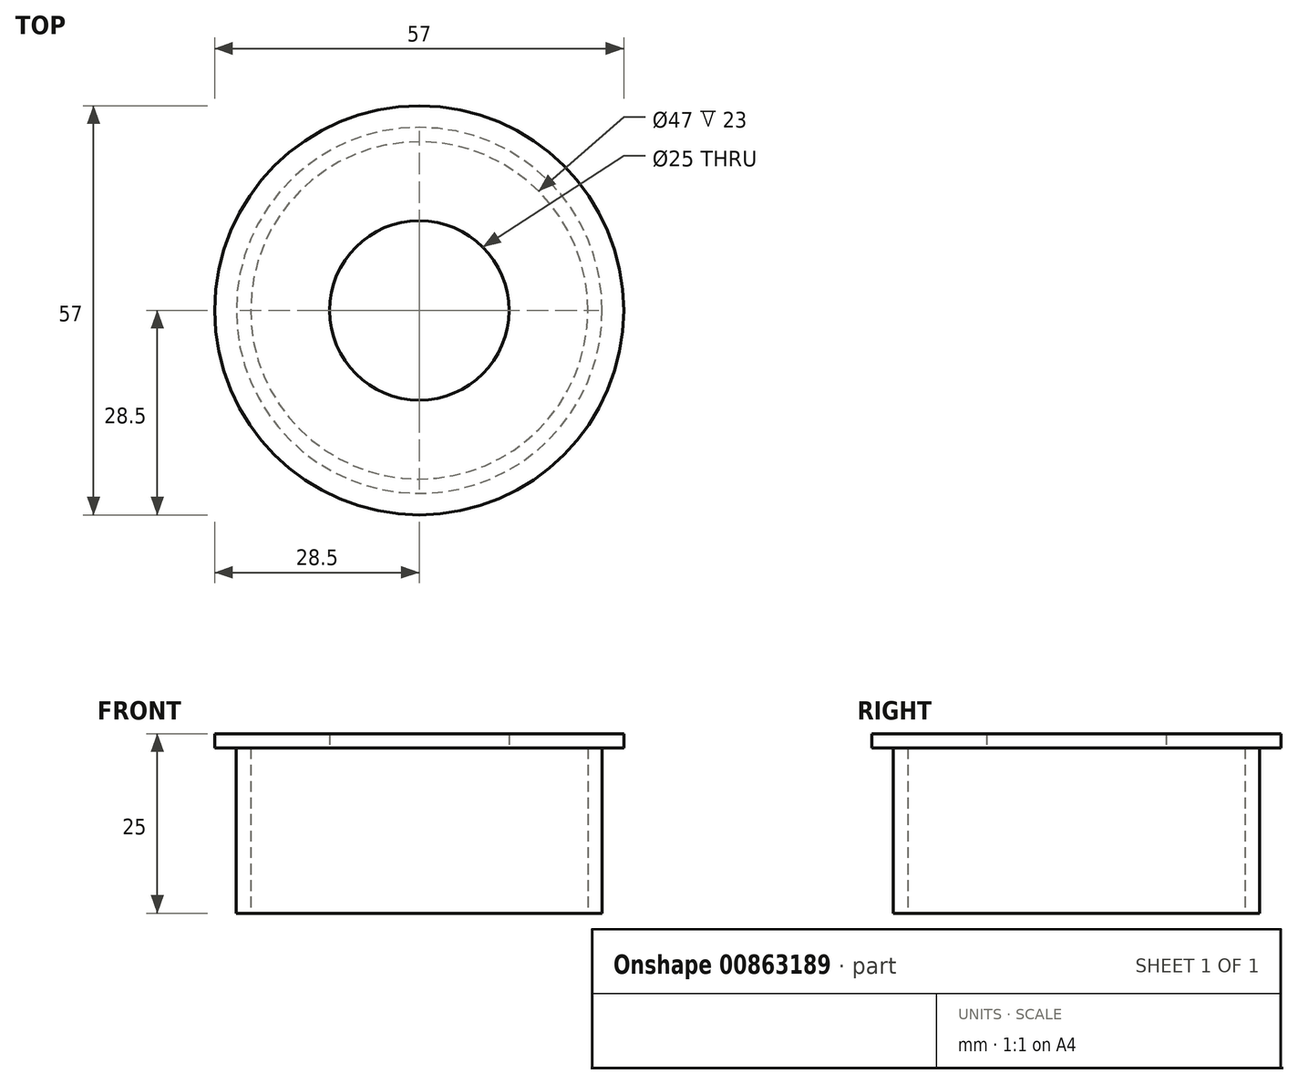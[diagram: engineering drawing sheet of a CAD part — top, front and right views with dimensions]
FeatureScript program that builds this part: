
annotation { "Feature Type Name" : "Feature", "Feature Type Description" : "" }
export const myFeature = defineFeature(function(context is Context, id is Id, definition is map)
    precondition{}
    {
        {
            var Q0;
            Q0=qCreatedBy(makeId("Top.planeOp"),FACE);
            var sketch = newSketch(context, id + "F0", { "sketchPlane" : qUnion([Q0])});
            skCircle(sketch, "E0", {"center": v(0, 0) * mm, "radius": 25.5 * mm});
            skCircle(sketch, "E1", {"center": v(0, 0) * mm, "radius": 12.5 * mm});
            skCircle(sketch, "E2.0", {"center": v(0, 0) * mm, "radius": 28.5 * mm});
            skSolve(sketch);
        }
        {
            var Q0;
            Q0=makeQuery(id+"F0.imprint","IMPRINT",FACE,{"disambiguationData":[TD([[makeQuery(id+"F0.imprint","IMPRINT",EDGE,{"derivedFrom":sQuery(id+"F0.wireOp",EDGE,"E0")}),1.0]])]});
            var Q1;
            Q1=makeQuery(id+"F0.imprint","IMPRINT",FACE,{"disambiguationData":[TD([[makeQuery(id+"F0.imprint","IMPRINT",EDGE,{"derivedFrom":sQuery(id+"F0.wireOp",EDGE,"E1")}),1.0]])]});
            extrude(context, id + "F1", {"entities" : qUnion([Q0, Q1]), "depth" : 25 * mm, "offsetDistance" : 25 * mm});
        }
        {
            var Q0;
            Q0=makeQuery(id+"F1.opExtrude","CAP_FACE",FACE,{"disambiguationData":[OSD([sQuery(id+"F0.wireOp",EDGE,"E0")])],"isStart":true});
            shell(context, id + "F2", {"entities" : qUnion([Q0]), "thickness" : 2 * mm});
        }
        {
            var Q0;
            Q0=makeQuery(id+"F0.imprint","IMPRINT",FACE,{"disambiguationData":[TD([[makeQuery(id+"F0.imprint","IMPRINT",EDGE,{"derivedFrom":sQuery(id+"F0.wireOp",EDGE,"E1")}),1.0]])]});
            var Q1;
            Q1=makeQuery(id+"F1.opExtrude","CAP_FACE",FACE,{"disambiguationData":[OSD([sQuery(id+"F0.wireOp",EDGE,"E0")])],"isStart":false});
            extrude(context, id + "F3", {"entities" : qUnion([Q0]), "operationType" : NewBodyOperationType.REMOVE, "endBound" : BoundingType.UP_TO_SURFACE, "depth" : 25 * mm, "endBoundEntityFace" : qUnion([Q1]), "offsetDistance" : 25 * mm});
        }
        {
            var Q0;
            Q0=makeQuery(id+"F1.opExtrude","CAP_FACE",FACE,{"disambiguationData":[OSD([sQuery(id+"F0.wireOp",EDGE,"E0")])],"isStart":false});
            var sketch = newSketch(context, id + "F4", { "sketchPlane" : qUnion([Q0])});
            skCircle(sketch, "E3.0", {"center": v(0, 0) * mm, "radius": 28.5 * mm});
            skSolve(sketch);
        }
        {
            var Q0;
            Q0=makeQuery(id+"F4.imprint","IMPRINT",FACE,{"disambiguationData":[TD([[makeQuery(id+"F4.imprint","IMPRINT",EDGE,{"derivedFrom":sQuery(id+"F4.wireOp",EDGE,"E3.0")}),1.0]])]});
            var Q1;
            Q1=sQuery(id+"F4.wireOp",EDGE,"E3.0");
            extrude(context, id + "F5", {"entities" : qUnion([Q0]), "operationType" : NewBodyOperationType.ADD, "surfaceEntities" : qUnion([Q1]), "oppositeDirection" : true, "depth" : 2 * mm, "offsetDistance" : 25 * mm});
        }
    });
